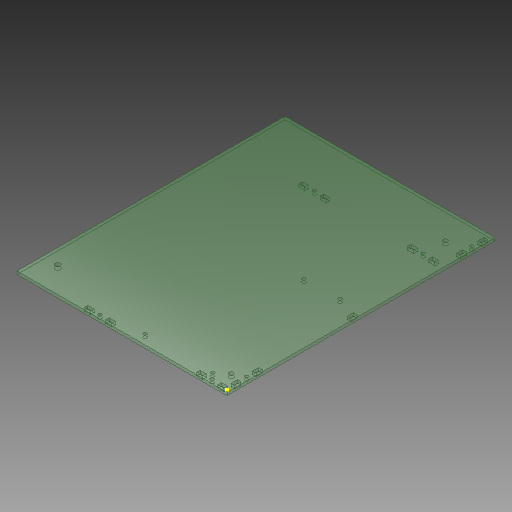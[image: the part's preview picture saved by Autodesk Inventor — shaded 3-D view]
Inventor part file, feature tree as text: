
AUTODESK INVENTOR PART (.ipt)
format: ipt  version: 2018 (Build 220112000, 112)  size: 807,424 bytes
history: native  units: mm
features: sketch x5, hole x3, projected_geometry x2, extrude x1
ambient origin geometry x8: Origin, YZ Plane, XZ Plane, XY Plane, X Axis, Y Axis, Z Axis, Center Point
bodies: Solid1 (feature_tree)
feature tree (11):
  extrude  "Extrusion1"  [1 undecoded]
  hole  "Hole2"  [1 undecoded]
  sketch  "Sketch3"  dims[d22=4.5mm d23=6.0mm d24=4.0mm d25=2.0mm d26=90.0deg d27=8.0mm d28=20.594885mm]
  hole  "Hole3"  [1 undecoded]
  hole  "Hole4"  [1 undecoded]
  sketch  "Sketch1"  dims[d0=3.0mm d1=0.0mm]
  sketch  "Sketch2"  dims[d15=3.4mm d16=6.0mm d17=4.0mm d18=2.0mm d19=90.0deg d20=8.0mm d21=20.594885mm]
  projected_geometry  "Projected Loop1"
  sketch  "Sketch4"  dims[d29=5.2mm d30=6.0mm d31=4.0mm d32=2.0mm d33=90.0deg d34=8.0mm d35=20.594885mm]
  projected_geometry  "Projected Loop2"
  sketch  "Sketch5"
note: 4 required parameter values undecoded (feature->parameter linkage not recoverable at this tier; creation-order binding heuristic only, values carry confidence <= 0.55)
